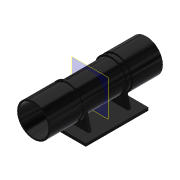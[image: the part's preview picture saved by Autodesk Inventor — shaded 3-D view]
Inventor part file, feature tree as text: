
AUTODESK INVENTOR PART (.ipt)
format: ipt  version: 2019.4 (Build 234330000, 330)  size: 179,200 bytes
history: native  units: mm
features: sketch x4, projected_geometry x4, extrude x3, mirror x2, revolve x1, plane x1
ambient origin geometry x8: Origin, YZ Plane, XZ Plane, XY Plane, X Axis, Y Axis, Z Axis, Center Point
bodies: Solid1 (feature_tree)
feature tree (15):
  revolve  "Revolution1"  [1 undecoded]
  extrude  "Extrusion1"  Depth=20.0mm
  mirror  "Mirror1"
  plane  "Work Plane1"
  extrude  "Extrusion2"  Depth=2.5mm
  mirror  "Mirror2"
  extrude  "Extrusion3"  TaperAngle=0.0deg  [1 undecoded]
  sketch  "Sketch1"  dims[d0=17.6mm d1=20.0mm]
  sketch  "Sketch2"  dims[d2=11.0mm d3=20.0mm]
  projected_geometry  "Projected Loop1"
  sketch  "Sketch3"  dims[d4=9.9mm d6=2.5mm]
  projected_geometry  "Projected Loop2"
  sketch  "Sketch4"  dims[d7=1.0mm d8=0.0mm d9=90.0deg d10=10.0mm d11=-0.872665mm d12=13.0mm d13=105.0deg d14=75.0deg d15=2.0mm d16=0.0mm d17=2.0mm d18=0.0mm]
  projected_geometry  "Projected Loop3"
  projected_geometry  "Projected Loop4"
note: 2 required parameter values undecoded (feature->parameter linkage not recoverable at this tier; creation-order binding heuristic only, values carry confidence <= 0.55)